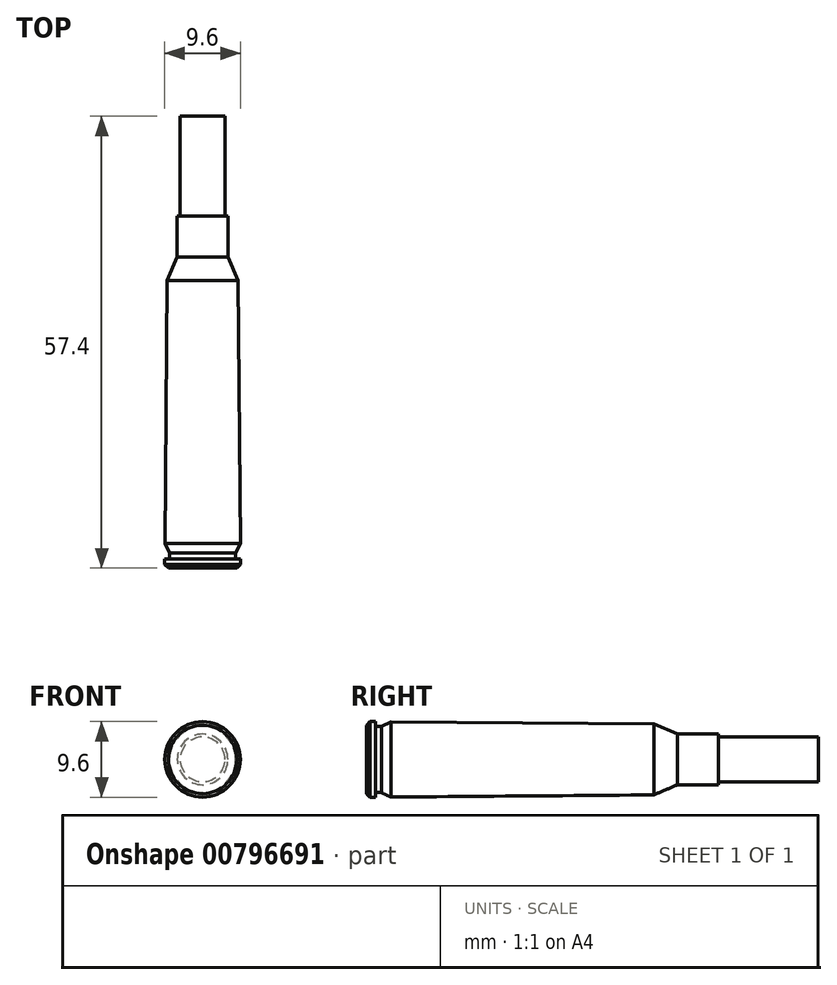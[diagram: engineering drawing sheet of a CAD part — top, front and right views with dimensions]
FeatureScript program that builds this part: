
annotation { "Feature Type Name" : "Feature", "Feature Type Description" : "" }
export const myFeature = defineFeature(function(context is Context, id is Id, definition is map)
    precondition{}
    {
        {
            var Q0;
            Q0=qCreatedBy(makeId("Right.planeOp"),FACE);
            var sketch = newSketch(context, id + "F0", { "sketchPlane" : qUnion([Q0])});
            skLineSegment(sketch, "E0", {"start": v(0, 0) * mm, "end": v(0.45, 0) * mm});
            skLineSegment(sketch, "E1", {"start": v(0, -4.35) * mm, "end": v(1.14, -4.35) * mm});
            skLineSegment(sketch, "E2", {"start": v(0, -6.59) * mm, "end": v(3.13, -6.59) * mm});
            skLineSegment(sketch, "E3", {"start": v(0, -10.21) * mm, "end": v(36.52, -10.21) * mm});
            skLineSegment(sketch, "E4", {"start": v(0, -14.09) * mm, "end": v(39.55, -14.09) * mm});
            skLineSegment(sketch, "E5", {"start": v(0, -19) * mm, "end": v(44.7, -19) * mm});
            skLineSegment(sketch, "E6", {"start": v(0, -23) * mm, "end": v(57.4, -23) * mm});
            skLineSegment(sketch, "E7", {"start": v(0.45, 0) * mm, "end": v(1.14, 0) * mm});
            skLineSegment(sketch, "E8", {"start": v(1.14, 0) * mm, "end": v(1.9, 0) * mm});
            skLineSegment(sketch, "E9", {"start": v(1.9, 0) * mm, "end": v(3.13, 0) * mm});
            skLineSegment(sketch, "E10", {"start": v(3.13, 0) * mm, "end": v(36.52, 0) * mm});
            skLineSegment(sketch, "E11", {"start": v(36.52, 0) * mm, "end": v(39.55, 0) * mm});
            skLineSegment(sketch, "E12", {"start": v(39.55, 0) * mm, "end": v(44.7, 0) * mm});
            skLineSegment(sketch, "E13", {"start": v(44.7, 0) * mm, "end": v(57.4, 0) * mm});
            skLineSegment(sketch, "E14", {"start": v(57.4, 0) * mm, "end": v(57.4, 2.85) * mm});
            skLineSegment(sketch, "E15", {"start": v(57.4, 2.85) * mm, "end": v(44.7, 2.85) * mm});
            skLineSegment(sketch, "E16", {"start": v(44.7, 0) * mm, "end": v(44.7, 3.21) * mm});
            skLineSegment(sketch, "E17", {"start": v(44.7, 3.21) * mm, "end": v(39.55, 3.21) * mm});
            skLineSegment(sketch, "E18", {"start": v(39.55, 3.21) * mm, "end": v(36.52, 4.5) * mm});
            skLineSegment(sketch, "E19", {"start": v(36.52, 4.5) * mm, "end": v(36.52, 0) * mm});
            skLineSegment(sketch, "E20", {"start": v(36.52, 4.5) * mm, "end": v(3.13, 4.79) * mm});
            skLineSegment(sketch, "E21", {"start": v(3.13, 4.8) * mm, "end": v(3.13, 0) * mm});
            skLineSegment(sketch, "E22", {"start": v(3.13, 4.79) * mm, "end": v(1.9, 4.21) * mm});
            skLineSegment(sketch, "E23", {"start": v(1.9, 4.21) * mm, "end": v(1.9, 0) * mm});
            skLineSegment(sketch, "E24", {"start": v(1.9, 4.21) * mm, "end": v(1.14, 4.21) * mm});
            skLineSegment(sketch, "E25", {"start": v(1.14, 0) * mm, "end": v(1.14, 4.8) * mm});
            skLineSegment(sketch, "E26", {"start": v(1.14, 4.8) * mm, "end": v(0.45, 4.8) * mm});
            skLineSegment(sketch, "E27", {"start": v(0.45, 4.8) * mm, "end": v(0, 4.35) * mm});
            skLineSegment(sketch, "E28", {"start": v(0, 4.35) * mm, "end": v(0, 0) * mm});
            skSolve(sketch);
        }
        {
            var Q0;
            Q0=makeQuery(id+"F0.imprint","IMPRINT",FACE,{"disambiguationData":[TD([[makeQuery(id+"F0.imprint","IMPRINT",EDGE,{"derivedFrom":sQuery(id+"F0.wireOp",EDGE,"E0")}),1.0]])]});
            var Q1;
            {var subQ0=sQuery(id+"F0.wireOp",EDGE,"E8");Q1=makeQuery(id+"F0.imprint","IMPRINT",FACE,{"disambiguationData":[TD([[makeQuery(id+"F0.imprint","IMPRINT",EDGE,{"derivedFrom":subQ0}),1.0]])]});}
            var Q2;
            Q2=makeQuery(id+"F0.imprint","IMPRINT",FACE,{"disambiguationData":[TD([[makeQuery(id+"F0.imprint","IMPRINT",EDGE,{"derivedFrom":sQuery(id+"F0.wireOp",EDGE,"E9")}),1.0]])]});
            var Q3;
            Q3=makeQuery(id+"F0.imprint","IMPRINT",FACE,{"disambiguationData":[TD([[makeQuery(id+"F0.imprint","IMPRINT",EDGE,{"derivedFrom":sQuery(id+"F0.wireOp",EDGE,"E10")}),1.0]])]});
            var Q4;
            Q4=makeQuery(id+"F0.imprint","IMPRINT",FACE,{"disambiguationData":[TD([[makeQuery(id+"F0.imprint","IMPRINT",EDGE,{"derivedFrom":sQuery(id+"F0.wireOp",EDGE,"E11")}),1.0]])]});
            var Q5;
            {var subQ0=sQuery(id+"F0.wireOp",EDGE,"E13");Q5=makeQuery(id+"F0.imprint","IMPRINT",FACE,{"disambiguationData":[TD([[makeQuery(id+"F0.imprint","IMPRINT",EDGE,{"derivedFrom":subQ0}),1.0]])]});}
            var Q6;
            Q6=sQuery(id+"F0.wireOp",EDGE,"E10");
            revolve(context, id + "F1", {"surfaceOperationType" : NewSurfaceOperationType.NEW, "entities" : qUnion([Q0, Q1, Q2, Q3, Q4, Q5]), "axis" : qUnion([Q6]), "revolveType" : RevolveType.FULL});
        }
    });
